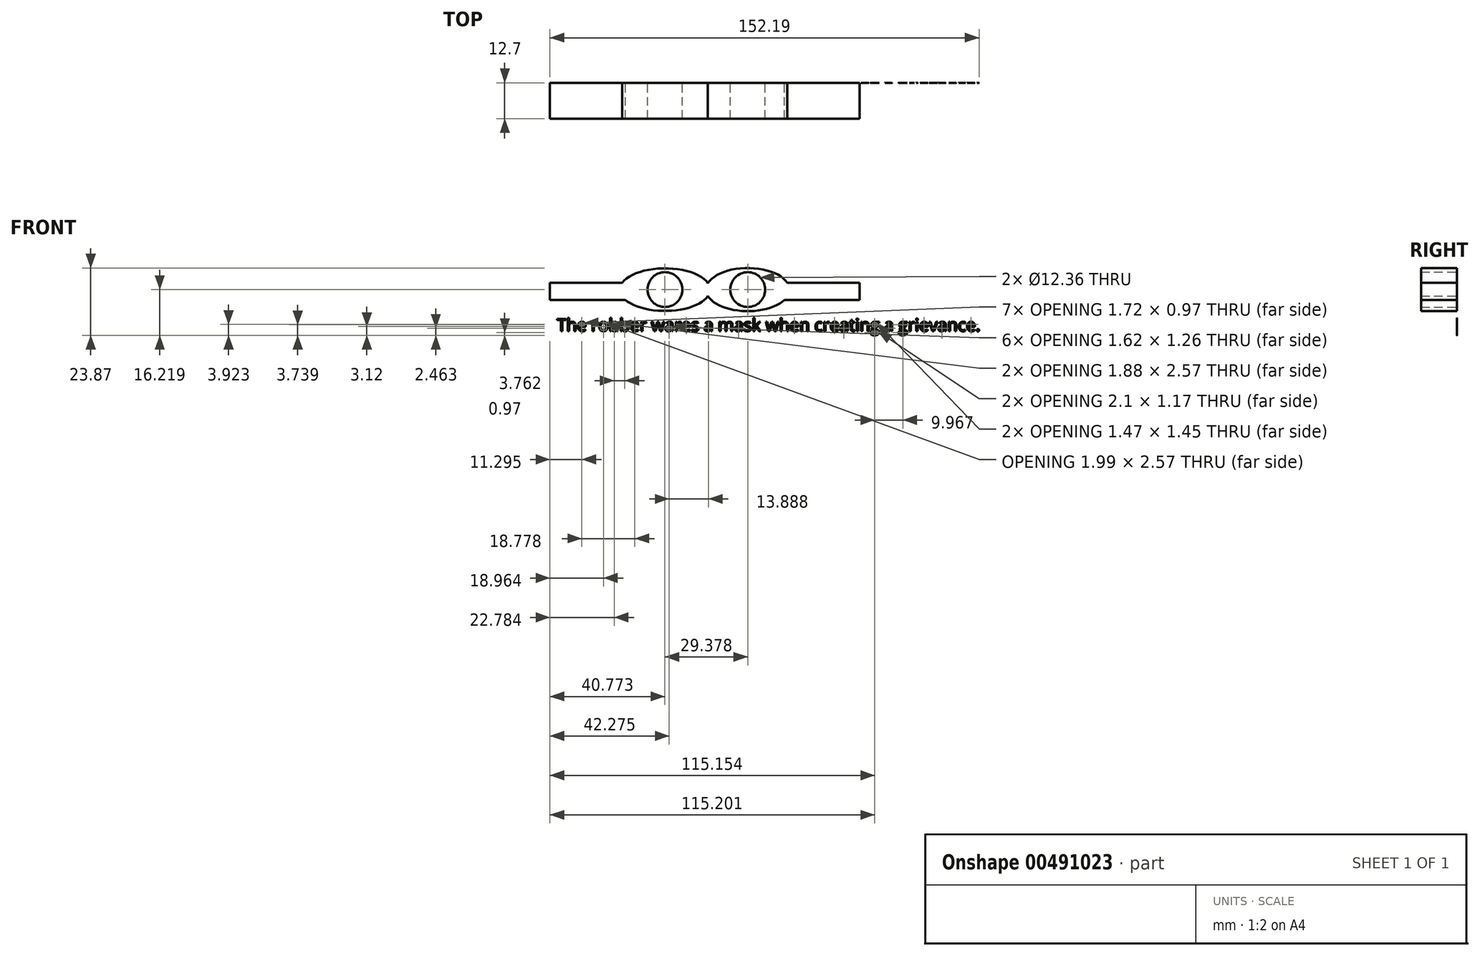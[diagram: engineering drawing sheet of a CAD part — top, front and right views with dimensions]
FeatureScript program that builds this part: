
annotation { "Feature Type Name" : "Feature", "Feature Type Description" : "" }
export const myFeature = defineFeature(function(context is Context, id is Id, definition is map)
    precondition{}
    {
        {
            var Q0;
            Q0=qCreatedBy(makeId("Front.planeOp"),FACE);
            var sketch = newSketch(context, id + "F0", { "sketchPlane" : qUnion([Q0])});
            skCircle(sketch, "E0", {"center": v(-15.29, 8.14) * mm, "radius": 6.18 * mm});
            skCircle(sketch, "E1", {"center": v(14.1, 8.14) * mm, "radius": 6.18 * mm});
            skEllipse(sketch, "E2", {"center": v(-15.29, 8.14) * mm, "majorRadius": 16 * mm, "minorRadius": 7.55 * mm, "majorAxis": v(1, 0)});
            skEllipse(sketch, "E3", {"center": v(14.1, 8.14) * mm, "majorRadius": 14.8 * mm, "minorRadius": 7.65 * mm, "majorAxis": v(1, 0)});
            skLineSegment(sketch, "E4", {"start": v(-30.42, 10.6) * mm, "end": v(-56.06, 10.6) * mm});
            skLineSegment(sketch, "E5", {"start": v(-56.06, 10.6) * mm, "end": v(-56.06, 4.52) * mm});
            skLineSegment(sketch, "E6", {"start": v(-56.06, 4.52) * mm, "end": v(-29.34, 4.52) * mm});
            skLineSegment(sketch, "E7", {"start": v(27.13, 4.52) * mm, "end": v(53.75, 4.52) * mm});
            skLineSegment(sketch, "E8", {"start": v(53.75, 4.52) * mm, "end": v(53.75, 10.6) * mm});
            skLineSegment(sketch, "E9", {"start": v(53.75, 10.6) * mm, "end": v(28.1, 10.6) * mm});
            skSolve(sketch);
        }
        {
            var Q0;
            {var subQ0=sQuery(id+"F0.wireOp",EDGE,"E4");Q0=makeQuery(id+"F0.imprint","IMPRINT",FACE,{"disambiguationData":[TD([[makeQuery(id+"F0.imprint","IMPRINT",EDGE,{"derivedFrom":subQ0}),1.0]])]});}
            var Q1;
            Q1=makeQuery(id+"F0.imprint","IMPRINT",FACE,{"disambiguationData":[TD([[makeQuery(id+"F0.imprint","IMPRINT",EDGE,{"derivedFrom":sQuery(id+"F0.wireOp",EDGE,"E0")}),-1.0]])]});
            var Q2;
            {var subQ0=sQuery(id+"F0.wireOp",EDGE,"E3");var subQ1=sQuery(id+"F0.wireOp",EDGE,"E2");var subQ2=makeQuery(id+"F0.imprint","INTERSECT",VERTEX,{"disambiguationData":[OD(0.0)],"derivedFrom":[subQ1,subQ0]});Q2=makeQuery(id+"F0.imprint","IMPRINT",FACE,{"disambiguationData":[TD([[makeQuery(id+"F0.imprint","IMPRINT",EDGE,{"disambiguationData":[TD([[subQ2,1.0]])],"derivedFrom":subQ1}),1.0]])]});}
            var Q3;
            Q3=makeQuery(id+"F0.imprint","IMPRINT",FACE,{"disambiguationData":[TD([[makeQuery(id+"F0.imprint","IMPRINT",EDGE,{"derivedFrom":sQuery(id+"F0.wireOp",EDGE,"E1")}),-1.0]])]});
            var Q4;
            {var subQ0=sQuery(id+"F0.wireOp",EDGE,"E7");Q4=makeQuery(id+"F0.imprint","IMPRINT",FACE,{"disambiguationData":[TD([[makeQuery(id+"F0.imprint","IMPRINT",EDGE,{"derivedFrom":subQ0}),1.0]])]});}
            extrude(context, id + "F1", {"entities" : qUnion([Q0, Q1, Q2, Q3, Q4]), "depth" : 12.7 * mm});
        }
        {
            var Q0;
            Q0=qCreatedBy(makeId("Front.planeOp"),FACE);
            var sketch = newSketch(context, id + "F2", { "sketchPlane" : qUnion([Q0])});
            skText(sketch, "E10", { "text": "The robber wares a mask when creating a grievance. ", "fontName": "OpenSans-Regular.ttf"});
            const initialGuessF2  = {"E10": [-0.05366, -0.0066, 1, 0, 0.00442]};
            skSetInitialGuess(sketch, initialGuessF2);
            skSolve(sketch);
        }
        {
            var Q0;
            Q0 = qSketchRegion(id + "F2", true);
            extrude(context, id + "F3", {"entities" : qUnion([Q0]), "depth" : 0.05 * mm});
        }
    });
